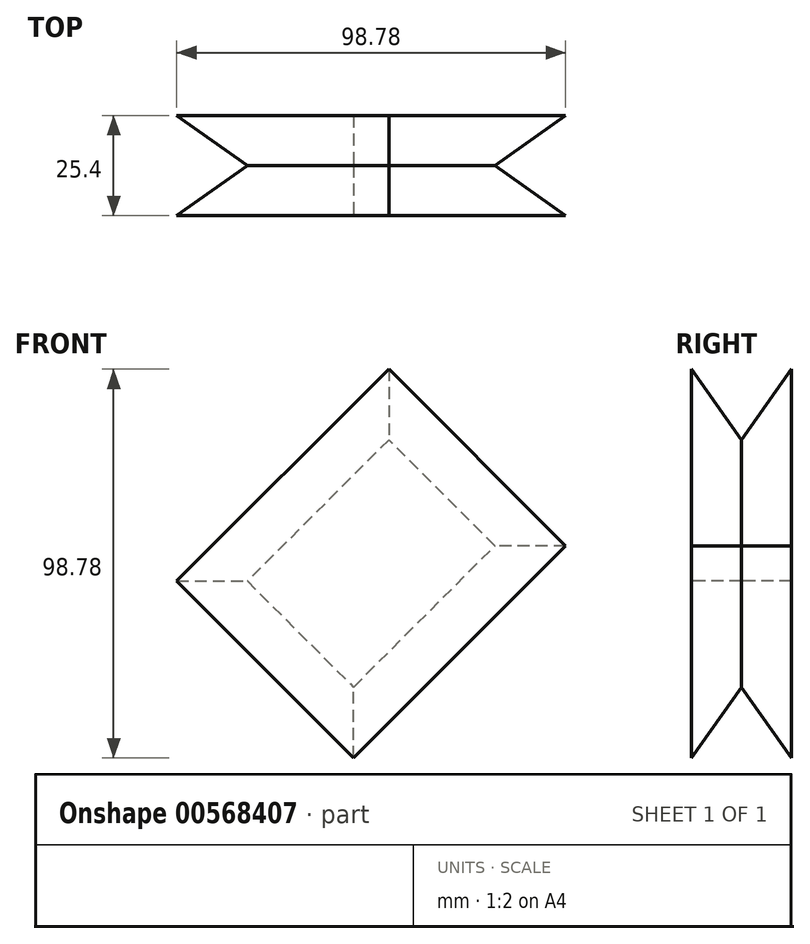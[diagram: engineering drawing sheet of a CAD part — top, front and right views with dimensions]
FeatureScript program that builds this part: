
annotation { "Feature Type Name" : "Feature", "Feature Type Description" : "" }
export const myFeature = defineFeature(function(context is Context, id is Id, definition is map)
    precondition{}
    {
        {
            var Q0;
            Q0=qCreatedBy(makeId("Front.planeOp"),FACE);
            var sketch = newSketch(context, id + "F0", { "sketchPlane" : qUnion([Q0])});
            skLineSegment(sketch, "E0", {"start": v(0, 0) * mm, "end": v(-26.94, 26.94) * mm});
            skLineSegment(sketch, "E1", {"start": v(-26.94, 26.94) * mm, "end": v(8.98, 62.86) * mm});
            skLineSegment(sketch, "E2", {"start": v(8.98, 62.86) * mm, "end": v(35.92, 35.92) * mm});
            skLineSegment(sketch, "E3", {"start": v(35.92, 35.92) * mm, "end": v(0, 0) * mm});
            skLineSegment(sketch, "E4", {"start": v(0, 0) * mm, "end": v(39.02, 0) * mm, "construction": true});
            skSolve(sketch);
        }
        {
            var Q0;
            Q0=makeQuery(id+"F0.imprint","IMPRINT",FACE,{"disambiguationData":[TD([[makeQuery(id+"F0.imprint","IMPRINT",EDGE,{"derivedFrom":sQuery(id+"F0.wireOp",EDGE,"E0")}),-1.0]])]});
            extrude(context, id + "F1", {"entities" : qUnion([Q0]), "endBound" : BoundingType.SYMMETRIC, "oppositeDirection" : true, "depth" : 25.4 * mm, "offsetDistance" : 25.4 * mm, "hasDraft" : true, "draftAngle" : 45 * degree});
        }
    });
